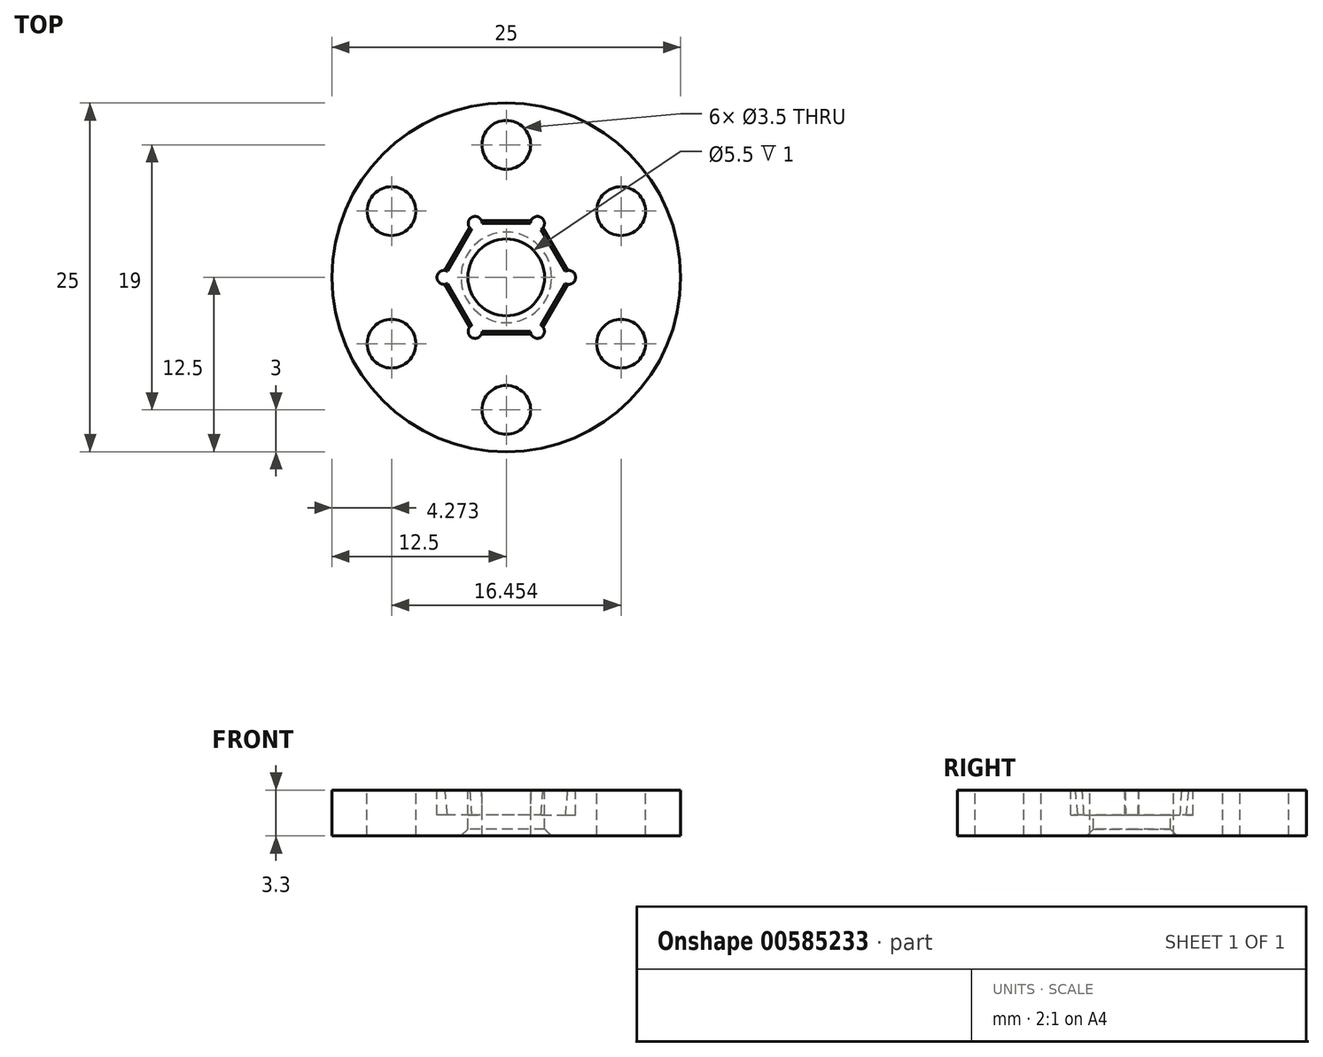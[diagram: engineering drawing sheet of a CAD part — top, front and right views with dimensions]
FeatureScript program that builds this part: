
annotation { "Feature Type Name" : "Feature", "Feature Type Description" : "" }
export const myFeature = defineFeature(function(context is Context, id is Id, definition is map)
    precondition{}
    {
        {
            var Q0;
            Q0=qCreatedBy(makeId("Top.planeOp"),FACE);
            var sketch = newSketch(context, id + "F0", { "sketchPlane" : qUnion([Q0])});
            skCircle(sketch, "E0", {"center": v(0, 0) * mm, "radius": 12.5 * mm});
            skCircle(sketch, "E1", {"center": v(0, 0) * mm, "radius": 2.75 * mm});
            skCircle(sketch, "E2.cCircle", {"center": v(0, 0) * mm, "radius": 3.85 * mm, "construction": true});
            skLineSegment(sketch, "E2.0", {"start": v(-2.22, 3.85) * mm, "end": v(2.22, 3.85) * mm});
            skLineSegment(sketch, "E2.1", {"start": v(2.22, 3.85) * mm, "end": v(4.45, 0) * mm});
            skLineSegment(sketch, "E2.2", {"start": v(4.45, 0) * mm, "end": v(2.22, -3.85) * mm});
            skLineSegment(sketch, "E2.3", {"start": v(2.22, -3.85) * mm, "end": v(-2.22, -3.85) * mm});
            skLineSegment(sketch, "E2.4", {"start": v(-2.22, -3.85) * mm, "end": v(-4.45, 0) * mm});
            skLineSegment(sketch, "E2.5", {"start": v(-4.45, 0) * mm, "end": v(-2.22, 3.85) * mm});
            skPoint(sketch, "E2.0.midPoint", {"position": v(0, 3.85) * mm});
            skCircle(sketch, "E3", {"center": v(0, 9.5) * mm, "radius": 1.75 * mm});
            skLineSegment(sketch, "E4", {"start": v(0, 9.5) * mm, "end": v(0, 0) * mm, "construction": true});
            skLineSegment(sketch, "E5", {"start": v(0, 0) * mm, "end": v(8.9, 0) * mm, "construction": true});
            skCircle(sketch, "E6.MirrorC", {"center": v(0, -9.5) * mm, "radius": 1.75 * mm});
            skCircle(sketch, "E7.1.0", {"center": v(8.23, 4.75) * mm, "radius": 1.75 * mm});
            skCircle(sketch, "E7.1.1", {"center": v(-8.23, -4.75) * mm, "radius": 1.75 * mm});
            skCircle(sketch, "E7.2.0", {"center": v(-8.23, 4.75) * mm, "radius": 1.75 * mm});
            skCircle(sketch, "E7.2.1", {"center": v(8.23, -4.75) * mm, "radius": 1.75 * mm});
            skSolve(sketch);
        }
        {
            var Q0;
            Q0 = qSketchRegion(id + "F0", true);
            var Q1;
            Q1=makeQuery(id+"F0.imprint","IMPRINT",FACE,{"disambiguationData":[TD([[makeQuery(id+"F0.imprint","IMPRINT",EDGE,{"derivedFrom":sQuery(id+"F0.wireOp",EDGE,"E1")}),-1.0]])]});
            extrude(context, id + "F1", {"entities" : qUnion([Q0, Q1]), "oppositeDirection" : true, "depth" : 1.5 * mm, "offsetDistance" : 25 * mm});
        }
        {
            var Q0;
            Q0 = qSketchRegion(id + "F0", true);
            var Q1;
            Q1=makeQuery(id+"F1.opExtrude","CAP_FACE",FACE,{"disambiguationData":[OSD([sQuery(id+"F0.wireOp",EDGE,"E0"),sQuery(id+"F0.wireOp",EDGE,"E1")])],"isStart":false});
            extrude(context, id + "F2", {"entities" : qUnion([Q0]), "operationType" : NewBodyOperationType.ADD, "depth" : 1.8 * mm, "offsetDistance" : 25 * mm});
        }
        {
            var Q0;
            Q0=makeQuery(id+"F2.opExtrude","CAP_EDGE",EDGE,{"disambiguationData":[OSD([sQuery(id+"F0.wireOp",EDGE,"E2.1")])],"isStart":false});
            var Q1;
            Q1=makeQuery(id+"F2.opExtrude","CAP_EDGE",EDGE,{"disambiguationData":[OSD([sQuery(id+"F0.wireOp",EDGE,"E2.0")])],"isStart":false});
            var Q2;
            Q2=makeQuery(id+"F2.opExtrude","CAP_EDGE",EDGE,{"disambiguationData":[OSD([sQuery(id+"F0.wireOp",EDGE,"E2.5")])],"isStart":false});
            var Q3;
            Q3=makeQuery(id+"F2.opExtrude","CAP_EDGE",EDGE,{"disambiguationData":[OSD([sQuery(id+"F0.wireOp",EDGE,"E2.4")])],"isStart":false});
            var Q4;
            Q4=makeQuery(id+"F2.opExtrude","CAP_EDGE",EDGE,{"disambiguationData":[OSD([sQuery(id+"F0.wireOp",EDGE,"E2.3")])],"isStart":false});
            var Q5;
            Q5=makeQuery(id+"F2.opExtrude","CAP_EDGE",EDGE,{"disambiguationData":[OSD([sQuery(id+"F0.wireOp",EDGE,"E2.2")])],"isStart":false});
            chamfer(context, id + "F3", {"entities" : qUnion([Q0, Q1, Q2, Q3, Q4, Q5]), "chamferType" : ChamferType.TWO_OFFSETS, "width1" : 0.2 * mm, "oppositeDirection" : false, "width2" : 2 * mm, "tangentPropagation" : true});
        }
        {
            var Q0;
            Q0=makeQuery(id+"F2.opExtrude","CAP_FACE",FACE,{"disambiguationData":[OSD([sQuery(id+"F0.wireOp",EDGE,"E0"),sQuery(id+"F0.wireOp",EDGE,"E2.0"),sQuery(id+"F0.wireOp",EDGE,"E2.1"),sQuery(id+"F0.wireOp",EDGE,"E2.2"),sQuery(id+"F0.wireOp",EDGE,"E2.3"),sQuery(id+"F0.wireOp",EDGE,"E2.4"),sQuery(id+"F0.wireOp",EDGE,"E2.5"),sQuery(id+"F0.wireOp",EDGE,"E3"),sQuery(id+"F0.wireOp",EDGE,"E6.MirrorC")])],"isStart":false});
            var sketch = newSketch(context, id + "F4", { "sketchPlane" : qUnion([Q0])});
            skCircle(sketch, "E8", {"center": v(-2.23, 3.87) * mm, "radius": 0.5 * mm});
            skCircle(sketch, "E9.1.0", {"center": v(-4.47, 0) * mm, "radius": 0.5 * mm});
            skCircle(sketch, "E9.2.0", {"center": v(-2.23, -3.87) * mm, "radius": 0.5 * mm});
            skCircle(sketch, "E9.3.0", {"center": v(2.23, -3.87) * mm, "radius": 0.5 * mm});
            skCircle(sketch, "E9.4.0", {"center": v(4.47, 0) * mm, "radius": 0.5 * mm});
            skCircle(sketch, "E9.5.0", {"center": v(2.23, 3.87) * mm, "radius": 0.5 * mm});
            skPoint(sketch, "E9.center", {"position": v(0, 0) * mm});
            skSolve(sketch);
        }
        {
            var Q0;
            Q0 = qSketchRegion(id + "F4", true);
            var Q1;
            Q1=makeQuery(id+"F3.opChamfer","BLEND_VERTEX",VERTEX,{"blendedFrom":[makeQuery(id+"F2.opExtrude","CAP_EDGE",EDGE,{"disambiguationData":[OSD([sQuery(id+"F0.wireOp",EDGE,"E2.0")])],"isStart":false}),makeQuery(id+"F2.opExtrude","CAP_EDGE",EDGE,{"disambiguationData":[OSD([sQuery(id+"F0.wireOp",EDGE,"E2.1")])],"isStart":false}),makeQuery(id+"F1.opExtrude","CAP_FACE",FACE,{"disambiguationData":[OSD([sQuery(id+"F0.wireOp",EDGE,"E0"),sQuery(id+"F0.wireOp",EDGE,"E1"),sQuery(id+"F0.wireOp",EDGE,"E3"),sQuery(id+"F0.wireOp",EDGE,"E6.MirrorC")])],"isStart":true})],"blendedInto":[makeQuery(id+"F1.opExtrude","CAP_FACE",FACE,{"disambiguationData":[OSD([sQuery(id+"F0.wireOp",EDGE,"E0"),sQuery(id+"F0.wireOp",EDGE,"E1"),sQuery(id+"F0.wireOp",EDGE,"E3"),sQuery(id+"F0.wireOp",EDGE,"E6.MirrorC")])],"isStart":true})]});
            extrude(context, id + "F5", {"entities" : qUnion([Q0]), "operationType" : NewBodyOperationType.REMOVE, "endBound" : BoundingType.UP_TO_VERTEX, "oppositeDirection" : true, "depth" : 25 * mm, "endBoundEntityVertex" : qUnion([Q1]), "offsetDistance" : 25 * mm});
        }
        {
            var Q0;
            Q0=makeQuery(id+"F1.opExtrude","CAP_EDGE",EDGE,{"disambiguationData":[OSD([sQuery(id+"F0.wireOp",EDGE,"E1")])],"isStart":false});
            chamfer(context, id + "F6", {"entities" : qUnion([Q0]), "width" : 0.5 * mm, "tangentPropagation" : true});
        }
    });
